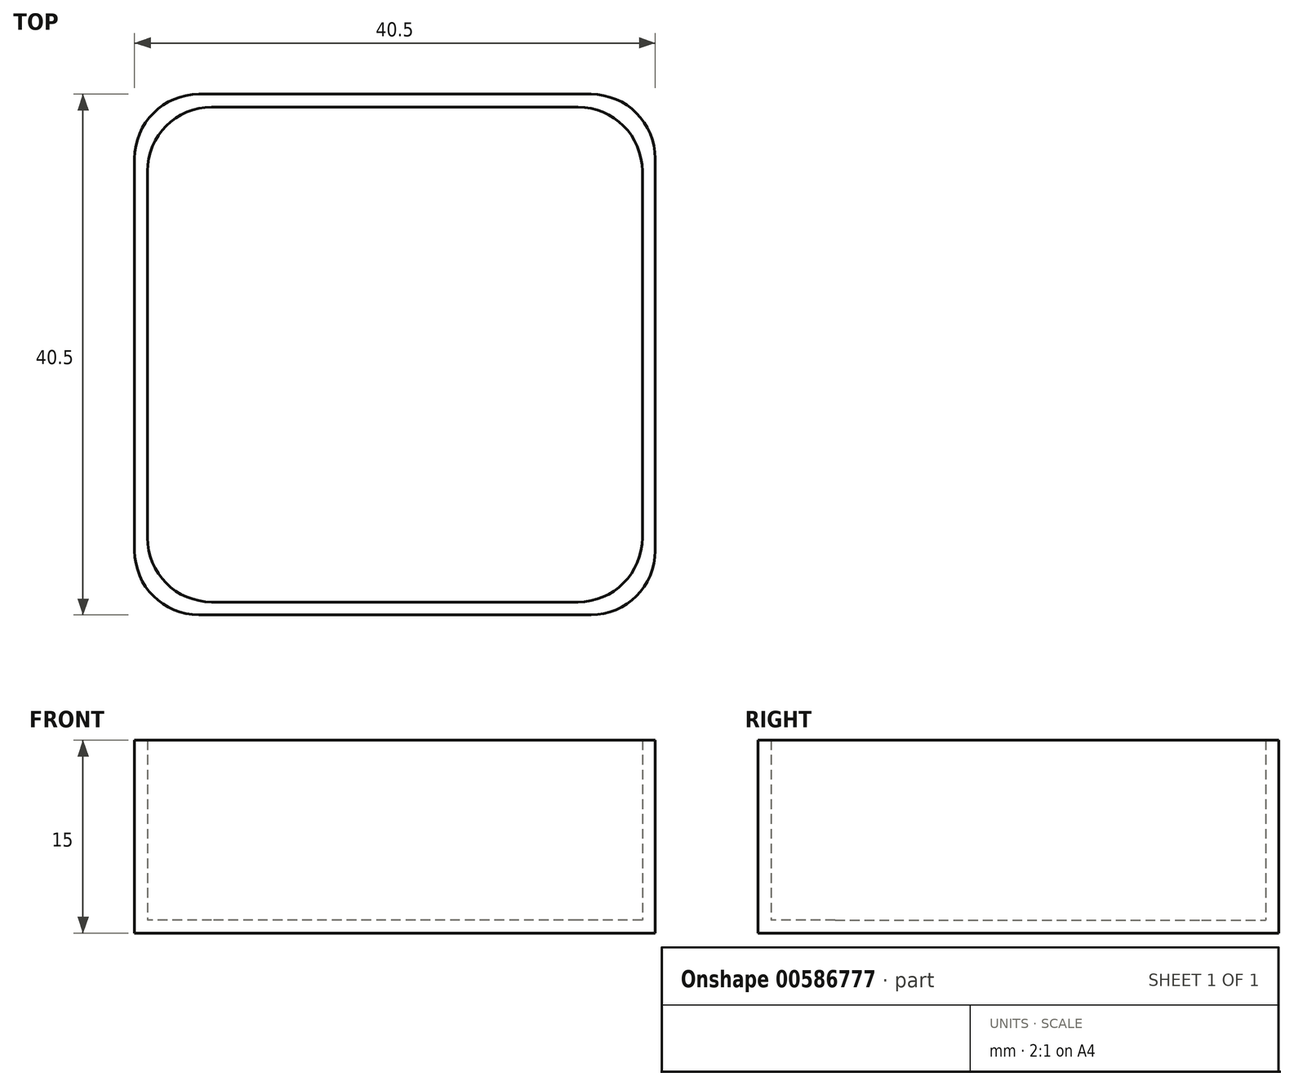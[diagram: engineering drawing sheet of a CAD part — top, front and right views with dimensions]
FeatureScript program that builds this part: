
annotation { "Feature Type Name" : "Feature", "Feature Type Description" : "" }
export const myFeature = defineFeature(function(context is Context, id is Id, definition is map)
    precondition{}
    {
        {
            var Q0;
            Q0=qCreatedBy(makeId("Top.planeOp"),FACE);
            var sketch = newSketch(context, id + "F0", { "sketchPlane" : qUnion([Q0])});
            skLineSegment(sketch, "E0.bottom", {"start": v(20.25, -20.25) * mm, "end": v(-20.25, -20.25) * mm});
            skLineSegment(sketch, "E0.top", {"start": v(20.25, 20.25) * mm, "end": v(-20.25, 20.25) * mm});
            skLineSegment(sketch, "E0.left", {"start": v(20.25, -20.25) * mm, "end": v(20.25, 20.25) * mm});
            skLineSegment(sketch, "E0.right", {"start": v(-20.25, -20.25) * mm, "end": v(-20.25, 20.25) * mm});
            skPoint(sketch, "E0.middle", {"position": v(0, 0) * mm});
            skLineSegment(sketch, "E1.bottom", {"start": v(19.25, -19.25) * mm, "end": v(-19.25, -19.25) * mm});
            skLineSegment(sketch, "E1.top", {"start": v(19.25, 19.25) * mm, "end": v(-19.25, 19.25) * mm});
            skLineSegment(sketch, "E1.left", {"start": v(19.25, -19.25) * mm, "end": v(19.25, 19.25) * mm});
            skLineSegment(sketch, "E1.right", {"start": v(-19.25, -19.25) * mm, "end": v(-19.25, 19.25) * mm});
            skSolve(sketch);
        }
        {
            var Q0;
            Q0=makeQuery(id+"F0.imprint","IMPRINT",FACE,{"disambiguationData":[TD([[makeQuery(id+"F0.imprint","IMPRINT",EDGE,{"derivedFrom":sQuery(id+"F0.wireOp",EDGE,"E1.bottom")}),-1.0]])]});
            extrude(context, id + "F1", {"entities" : qUnion([Q0]), "depth" : 1 * mm, "offsetDistance" : 25 * mm});
        }
        {
            var Q0;
            Q0=makeQuery(id+"F0.imprint","IMPRINT",FACE,{"disambiguationData":[TD([[makeQuery(id+"F0.imprint","IMPRINT",EDGE,{"derivedFrom":sQuery(id+"F0.wireOp",EDGE,"E0.bottom")}),-1.0]])]});
            extrude(context, id + "F2", {"entities" : qUnion([Q0]), "operationType" : NewBodyOperationType.ADD, "depth" : 15 * mm, "offsetDistance" : 25 * mm});
        }
        {
            var Q0;
            Q0=makeQuery(id+"F2.opExtrude","SWEPT_EDGE",EDGE,{"disambiguationData":[OSD([sQuery(id+"F0.wireOp",EDGE,"E0.bottom"),sQuery(id+"F0.wireOp",EDGE,"E0.left")])]});
            var Q1;
            Q1=makeQuery(id+"F2.opExtrude","SWEPT_EDGE",EDGE,{"disambiguationData":[OSD([sQuery(id+"F0.wireOp",EDGE,"E1.bottom"),sQuery(id+"F0.wireOp",EDGE,"E1.left")])]});
            var Q2;
            Q2=makeQuery(id+"F2.opExtrude","SWEPT_EDGE",EDGE,{"disambiguationData":[OSD([sQuery(id+"F0.wireOp",EDGE,"E1.bottom"),sQuery(id+"F0.wireOp",EDGE,"E1.right")])]});
            var Q3;
            Q3=makeQuery(id+"F2.opExtrude","SWEPT_EDGE",EDGE,{"disambiguationData":[OSD([sQuery(id+"F0.wireOp",EDGE,"E1.top"),sQuery(id+"F0.wireOp",EDGE,"E1.right")])]});
            var Q4;
            Q4=makeQuery(id+"F2.opExtrude","SWEPT_EDGE",EDGE,{"disambiguationData":[OSD([sQuery(id+"F0.wireOp",EDGE,"E1.top"),sQuery(id+"F0.wireOp",EDGE,"E1.left")])]});
            var Q5;
            Q5=makeQuery(id+"F2.opExtrude","SWEPT_EDGE",EDGE,{"disambiguationData":[OSD([sQuery(id+"F0.wireOp",EDGE,"E0.bottom"),sQuery(id+"F0.wireOp",EDGE,"E0.right")])]});
            var Q6;
            Q6=makeQuery(id+"F2.opExtrude","SWEPT_EDGE",EDGE,{"disambiguationData":[OSD([sQuery(id+"F0.wireOp",EDGE,"E0.top"),sQuery(id+"F0.wireOp",EDGE,"E0.right")])]});
            var Q7;
            Q7=makeQuery(id+"F2.opExtrude","SWEPT_EDGE",EDGE,{"disambiguationData":[OSD([sQuery(id+"F0.wireOp",EDGE,"E0.top"),sQuery(id+"F0.wireOp",EDGE,"E0.left")])]});
            fillet(context, id + "F3", {"entities" : qUnion([Q0, Q1, Q2, Q3, Q4, Q5, Q6, Q7]), "radius" : 5 * mm, "tangentPropagation" : true, "allowEdgeOverflow" : false});
        }
    });
